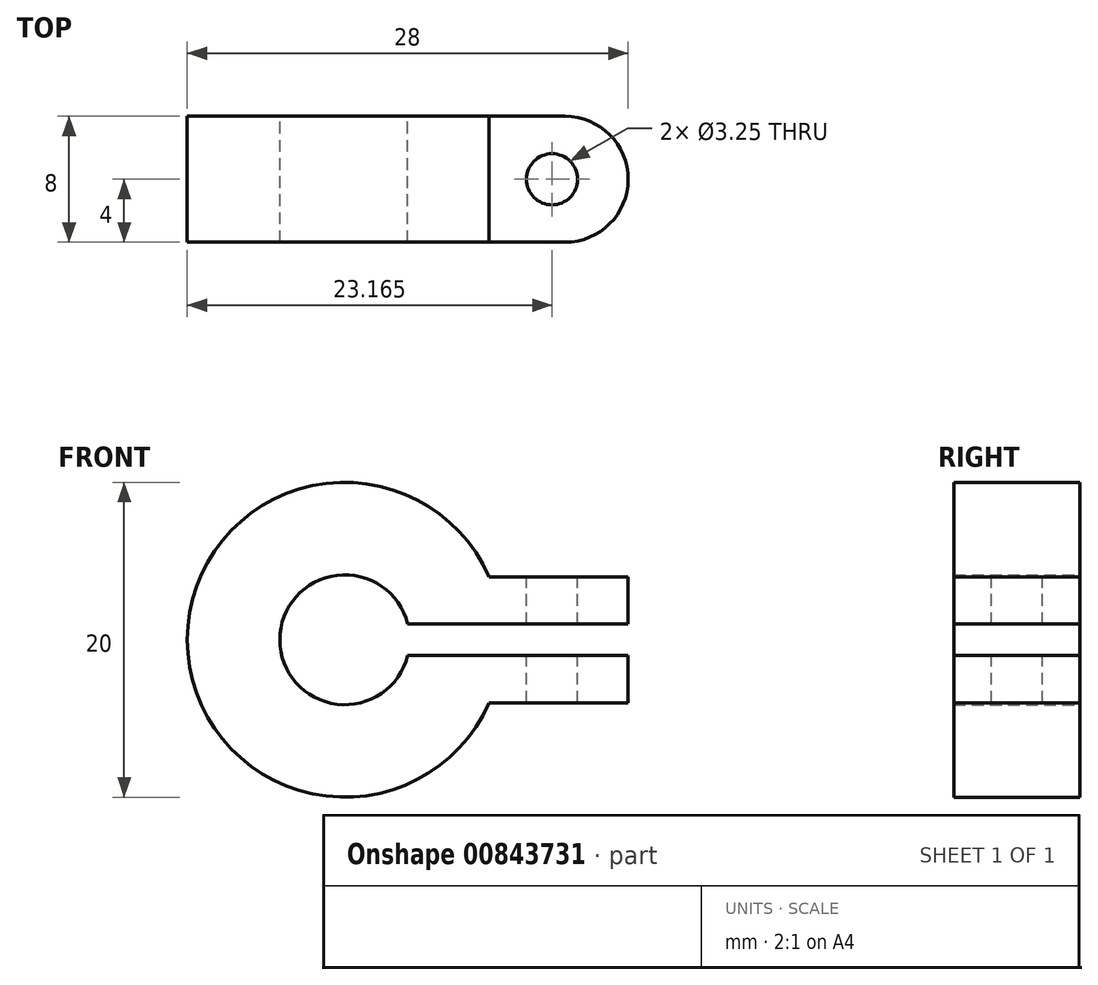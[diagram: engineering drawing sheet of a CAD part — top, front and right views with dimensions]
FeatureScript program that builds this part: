
annotation { "Feature Type Name" : "Feature", "Feature Type Description" : "" }
export const myFeature = defineFeature(function(context is Context, id is Id, definition is map)
    precondition{}
    {
        {
            var Q0;
            Q0=qCreatedBy(makeId("Front.planeOp"),FACE);
            var sketch = newSketch(context, id + "F0", { "sketchPlane" : qUnion([Q0])});
            skArc(sketch, "E0", {"start": v(4, 1) * mm, "mid": v(-4.12, 0) * mm, "end": v(4, -1) * mm});
            skArc(sketch, "E1", {"start": v(9.17, 4) * mm, "mid": v(-10, 0) * mm, "end": v(9.17, -4) * mm});
            skLineSegment(sketch, "E2.bottom", {"start": v(9.17, 4) * mm, "end": v(18, 4) * mm});
            skLineSegment(sketch, "E2.right", {"start": v(18, 4) * mm, "end": v(18, 1) * mm});
            skLineSegment(sketch, "E3.trimOffspring", {"start": v(9.17, -4) * mm, "end": v(18, -4) * mm});
            skLineSegment(sketch, "E4.bottom", {"start": v(4, 1) * mm, "end": v(18, 1) * mm});
            skLineSegment(sketch, "E4.top", {"start": v(4, -1) * mm, "end": v(18, -1) * mm});
            skLineSegment(sketch, "E5.trimOffspring", {"start": v(18, -1) * mm, "end": v(18, -4) * mm});
            skSolve(sketch);
        }
        {
            var Q0;
            Q0=makeQuery(id+"F0.imprint","IMPRINT",FACE,{"disambiguationData":[TD([[makeQuery(id+"F0.imprint","IMPRINT",EDGE,{"derivedFrom":sQuery(id+"F0.wireOp",EDGE,"E0")}),-1.0]])]});
            extrude(context, id + "F1", {"entities" : qUnion([Q0]), "depth" : 8 * mm, "offsetDistance" : 25 * mm});
        }
        {
            var Q0;
            Q0=makeQuery(id+"F1.opExtrude","SWEPT_FACE",FACE,{"disambiguationData":[OSD([sQuery(id+"F0.wireOp",EDGE,"E2.bottom")])]});
            var sketch = newSketch(context, id + "F2", { "sketchPlane" : qUnion([Q0])});
            skCircle(sketch, "E6", {"center": v(13.17, -4) * mm, "radius": 1.63 * mm});
            skSolve(sketch);
        }
        {
            var Q0;
            Q0=makeQuery(id+"F2.imprint","IMPRINT",FACE,{"disambiguationData":[TD([[makeQuery(id+"F2.imprint","IMPRINT",EDGE,{"derivedFrom":sQuery(id+"F2.wireOp",EDGE,"E6")}),1.0]])]});
            extrude(context, id + "F3", {"entities" : qUnion([Q0]), "operationType" : NewBodyOperationType.REMOVE, "endBound" : BoundingType.THROUGH_ALL, "oppositeDirection" : true, "depth" : 25 * mm, "offsetDistance" : 25 * mm});
        }
        {
            var Q0;
            Q0=makeQuery(id+"F1.opExtrude","CAP_EDGE",EDGE,{"disambiguationData":[OSD([sQuery(id+"F0.wireOp",EDGE,"E2.right")])],"isStart":false});
            var Q1;
            Q1=makeQuery(id+"F1.opExtrude","CAP_EDGE",EDGE,{"disambiguationData":[OSD([sQuery(id+"F0.wireOp",EDGE,"E5.trimOffspring")])],"isStart":false});
            var Q2;
            Q2=makeQuery(id+"F1.opExtrude","CAP_EDGE",EDGE,{"disambiguationData":[OSD([sQuery(id+"F0.wireOp",EDGE,"E5.trimOffspring")])],"isStart":true});
            var Q3;
            Q3=makeQuery(id+"F1.opExtrude","CAP_EDGE",EDGE,{"disambiguationData":[OSD([sQuery(id+"F0.wireOp",EDGE,"E2.right")])],"isStart":true});
            fillet(context, id + "F4", {"entities" : qUnion([Q0, Q1, Q2, Q3]), "radius" : 4 * mm, "tangentPropagation" : true, "allowEdgeOverflow" : false});
        }
    });
